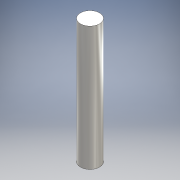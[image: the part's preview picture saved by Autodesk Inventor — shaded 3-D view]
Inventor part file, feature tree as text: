
AUTODESK INVENTOR PART (.ipt)
format: ipt  version: 2016 (Build 200138000, 138)  size: 89,600 bytes
history: native  units: mm
features: other x1, extrude x1, sketch x1
ambient origin geometry x8: Origin, YZ Plane, XZ Plane, XY Plane, X Axis, Y Axis, Z Axis, Center Point
bodies: Body1 (feature_tree)
feature tree (3):
  other  "ソリッド1"
  extrude  "押し出し1"  Depth=4.0mm
  sketch  "スケッチ1"
